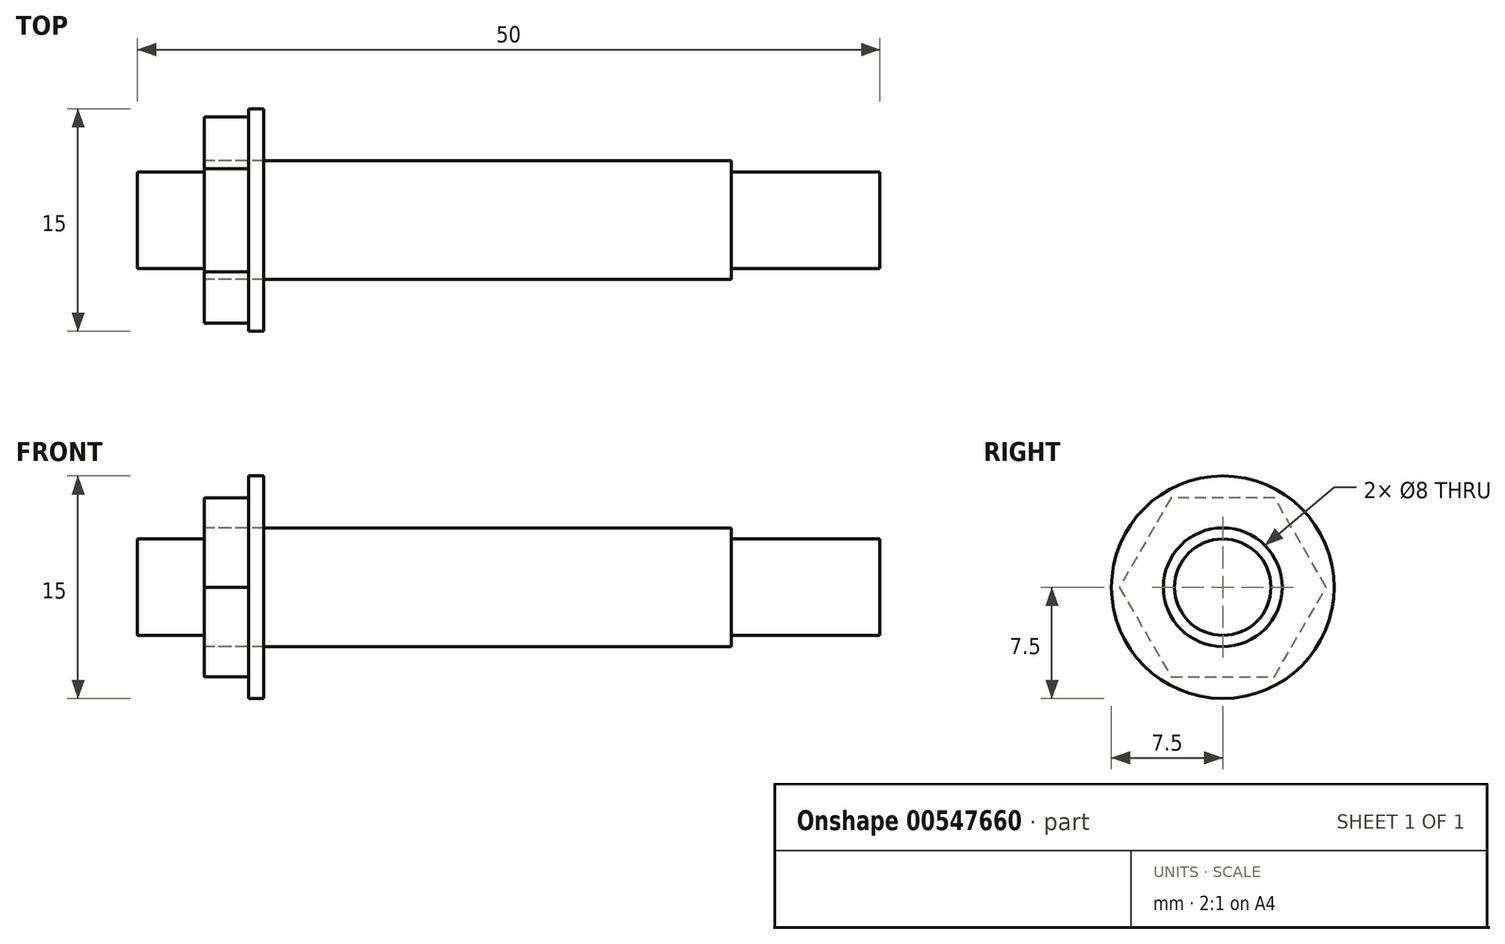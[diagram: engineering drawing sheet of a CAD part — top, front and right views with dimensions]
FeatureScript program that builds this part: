
annotation { "Feature Type Name" : "Feature", "Feature Type Description" : "" }
export const myFeature = defineFeature(function(context is Context, id is Id, definition is map)
    precondition{}
    {
        {
            var Q0;
            Q0=qCreatedBy(makeId("Front.planeOp"),FACE);
            var sketch = newSketch(context, id + "F0", { "sketchPlane" : qUnion([Q0])});
            skLineSegment(sketch, "E0", {"start": v(0, 0) * mm, "end": v(50, 0) * mm});
            skLineSegment(sketch, "E1", {"start": v(0, 0) * mm, "end": v(0, 3.25) * mm});
            skLineSegment(sketch, "E2", {"start": v(0, 3.25) * mm, "end": v(4.5, 3.25) * mm});
            skLineSegment(sketch, "E3", {"start": v(4.5, 3.25) * mm, "end": v(4.5, 4) * mm});
            skLineSegment(sketch, "E4", {"start": v(4.5, 4) * mm, "end": v(40, 4) * mm});
            skLineSegment(sketch, "E5", {"start": v(40, 4) * mm, "end": v(40, 3.25) * mm});
            skLineSegment(sketch, "E6", {"start": v(40, 3.25) * mm, "end": v(50, 3.25) * mm});
            skLineSegment(sketch, "E7", {"start": v(50, 3.25) * mm, "end": v(50, 0) * mm});
            skSolve(sketch);
        }
        {
            var Q0;
            Q0=makeQuery(id+"F0.imprint","IMPRINT",FACE,{"disambiguationData":[TD([[makeQuery(id+"F0.imprint","IMPRINT",EDGE,{"derivedFrom":sQuery(id+"F0.wireOp",EDGE,"E0")}),1.0]])]});
            var Q1;
            Q1=sQuery(id+"F0.wireOp",EDGE,"E0");
            revolve(context, id + "F1", {"entities" : qUnion([Q0]), "axis" : qUnion([Q1]), "revolveType" : RevolveType.FULL});
        }
        {
            var Q0;
            Q0=makeQuery(id+"F1.opRevolve","SWEPT_FACE",FACE,{"disambiguationData":[OSD([sQuery(id+"F0.wireOp",EDGE,"E3")])]});
            var sketch = newSketch(context, id + "F2", { "sketchPlane" : qUnion([Q0])});
            skCircle(sketch, "E8.0", {"center": v(0, 0) * mm, "radius": 4 * mm});
            skCircle(sketch, "E9.cCircle", {"center": v(0, 0) * mm, "radius": 6.03 * mm, "construction": true});
            skLineSegment(sketch, "E9.0", {"start": v(-3.48, 6.03) * mm, "end": v(3.48, 6.03) * mm});
            skLineSegment(sketch, "E9.1", {"start": v(3.48, 6.03) * mm, "end": v(6.96, 0) * mm});
            skLineSegment(sketch, "E9.2", {"start": v(6.96, 0) * mm, "end": v(3.48, -6.03) * mm});
            skLineSegment(sketch, "E9.3", {"start": v(3.48, -6.03) * mm, "end": v(-3.48, -6.03) * mm});
            skLineSegment(sketch, "E9.4", {"start": v(-3.48, -6.03) * mm, "end": v(-6.96, 0) * mm});
            skLineSegment(sketch, "E9.5", {"start": v(-6.96, 0) * mm, "end": v(-3.48, 6.03) * mm});
            skPoint(sketch, "E9.0.midPoint", {"position": v(0, 6.03) * mm});
            skSolve(sketch);
        }
        {
            var Q0;
            Q0=qSketchRegion(id+"F2",true);
            extrude(context, id + "F3", {"entities" : qUnion([Q0]), "oppositeDirection" : true, "depth" : 3 * mm});
        }
        {
            var Q0;
            Q0=makeQuery(id+"F3.opExtrude","CAP_FACE",FACE,{"disambiguationData":[OSD([sQuery(id+"F2.wireOp",EDGE,"E8.0"),sQuery(id+"F2.wireOp",EDGE,"E9.0"),sQuery(id+"F2.wireOp",EDGE,"E9.1"),sQuery(id+"F2.wireOp",EDGE,"E9.2"),sQuery(id+"F2.wireOp",EDGE,"E9.3"),sQuery(id+"F2.wireOp",EDGE,"E9.4"),sQuery(id+"F2.wireOp",EDGE,"E9.5")])],"isStart":false});
            var sketch = newSketch(context, id + "F4", { "sketchPlane" : qUnion([Q0])});
            skCircle(sketch, "E10.0", {"center": v(0, 0) * mm, "radius": 4 * mm});
            skCircle(sketch, "E11", {"center": v(0, 0) * mm, "radius": 7.5 * mm});
            skSolve(sketch);
        }
        {
            var Q0;
            Q0=qSketchRegion(id+"F4",true);
            extrude(context, id + "F5", {"entities" : qUnion([Q0]), "depth" : 1 * mm});
        }
    });
